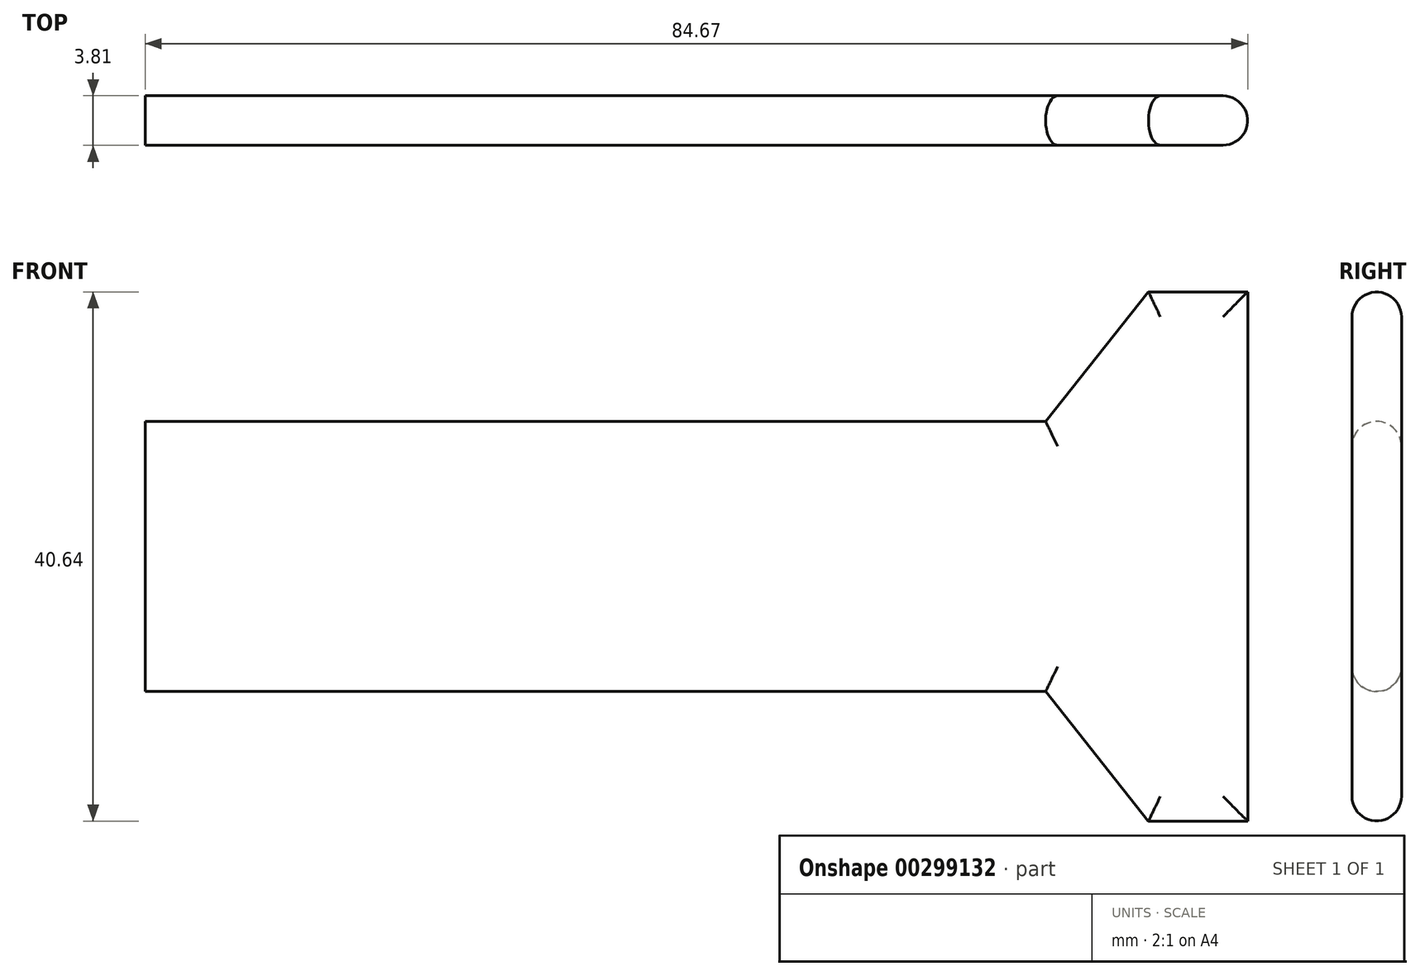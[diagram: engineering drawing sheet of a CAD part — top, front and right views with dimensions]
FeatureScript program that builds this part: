
annotation { "Feature Type Name" : "Feature", "Feature Type Description" : "" }
export const myFeature = defineFeature(function(context is Context, id is Id, definition is map)
    precondition{}
    {
        {
            var Q0;
            Q0=qCreatedBy(makeId("Front.planeOp"),FACE);
            var sketch = newSketch(context, id + "F0", { "sketchPlane" : qUnion([Q0])});
            skLineSegment(sketch, "E0", {"start": v(-30.4, 11.34) * mm, "end": v(38.74, 11.34) * mm});
            skLineSegment(sketch, "E1", {"start": v(38.74, 11.34) * mm, "end": v(38.74, -9.4) * mm});
            skLineSegment(sketch, "E2", {"start": v(38.74, -9.4) * mm, "end": v(-30.4, -9.4) * mm});
            skLineSegment(sketch, "E3", {"start": v(-30.4, -9.4) * mm, "end": v(-30.4, 11.34) * mm});
            skLineSegment(sketch, "E4", {"start": v(38.74, 11.34) * mm, "end": v(46.64, 21.29) * mm});
            skLineSegment(sketch, "E5", {"start": v(46.64, 21.29) * mm, "end": v(54.26, 21.29) * mm});
            skLineSegment(sketch, "E6", {"start": v(54.26, 21.29) * mm, "end": v(54.26, -19.35) * mm});
            skLineSegment(sketch, "E7", {"start": v(54.26, -19.35) * mm, "end": v(46.64, -19.35) * mm});
            skLineSegment(sketch, "E8", {"start": v(46.64, -19.35) * mm, "end": v(38.74, -9.4) * mm});
            skLineSegment(sketch, "E9", {"start": v(-30.4, 0) * mm, "end": v(38.74, 0) * mm});
            skSolve(sketch);
        }
        {
            var Q0;
            Q0=makeQuery(id+"F0.imprint","IMPRINT",FACE,{"disambiguationData":[TD([[makeQuery(id+"F0.imprint","IMPRINT",EDGE,{"derivedFrom":sQuery(id+"F0.wireOp",EDGE,"E1")}),1.0]])]});
            var Q1;
            {var subQ0=sQuery(id+"F0.wireOp",EDGE,"E0");Q1=makeQuery(id+"F0.imprint","IMPRINT",FACE,{"disambiguationData":[TD([[makeQuery(id+"F0.imprint","IMPRINT",EDGE,{"derivedFrom":subQ0}),-1.0]])]});}
            var Q2;
            {var subQ0=sQuery(id+"F0.wireOp",EDGE,"E2");Q2=makeQuery(id+"F0.imprint","IMPRINT",FACE,{"disambiguationData":[TD([[makeQuery(id+"F0.imprint","IMPRINT",EDGE,{"derivedFrom":subQ0}),-1.0]])]});}
            extrude(context, id + "F1", {"entities" : qUnion([Q0, Q1, Q2]), "depth" : 3.8 * mm});
        }
        {
            var Q0;
            Q0=makeQuery(id+"F1.opExtrude","CAP_EDGE",EDGE,{"disambiguationData":[OSD([sQuery(id+"F0.wireOp",EDGE,"E2")])],"isStart":true});
            var Q1;
            Q1=makeQuery(id+"F1.opExtrude","CAP_EDGE",EDGE,{"disambiguationData":[OSD([sQuery(id+"F0.wireOp",EDGE,"E0")])],"isStart":true});
            var Q2;
            Q2=makeQuery(id+"F1.opExtrude","CAP_EDGE",EDGE,{"disambiguationData":[OSD([sQuery(id+"F0.wireOp",EDGE,"E2")])],"isStart":false});
            var Q3;
            Q3=makeQuery(id+"F1.opExtrude","CAP_EDGE",EDGE,{"disambiguationData":[OSD([sQuery(id+"F0.wireOp",EDGE,"E0")])],"isStart":false});
            var Q4;
            Q4=makeQuery(id+"F1.opExtrude","CAP_EDGE",EDGE,{"disambiguationData":[OSD([sQuery(id+"F0.wireOp",EDGE,"E7")])],"isStart":false});
            var Q5;
            Q5=makeQuery(id+"F1.opExtrude","CAP_EDGE",EDGE,{"disambiguationData":[OSD([sQuery(id+"F0.wireOp",EDGE,"E7")])],"isStart":true});
            var Q6;
            Q6=makeQuery(id+"F1.opExtrude","CAP_EDGE",EDGE,{"disambiguationData":[OSD([sQuery(id+"F0.wireOp",EDGE,"E5")])],"isStart":true});
            var Q7;
            Q7=makeQuery(id+"F1.opExtrude","CAP_EDGE",EDGE,{"disambiguationData":[OSD([sQuery(id+"F0.wireOp",EDGE,"E5")])],"isStart":false});
            var Q8;
            Q8=makeQuery(id+"F1.opExtrude","CAP_EDGE",EDGE,{"disambiguationData":[OSD([sQuery(id+"F0.wireOp",EDGE,"E6")])],"isStart":false});
            var Q9;
            Q9=makeQuery(id+"F1.opExtrude","CAP_EDGE",EDGE,{"disambiguationData":[OSD([sQuery(id+"F0.wireOp",EDGE,"E6")])],"isStart":true});
            var Q10;
            Q10=makeQuery(id+"F1.opExtrude","CAP_EDGE",EDGE,{"disambiguationData":[OSD([sQuery(id+"F0.wireOp",EDGE,"E4")])],"isStart":false});
            var Q11;
            Q11=makeQuery(id+"F1.opExtrude","CAP_EDGE",EDGE,{"disambiguationData":[OSD([sQuery(id+"F0.wireOp",EDGE,"E8")])],"isStart":false});
            var Q12;
            Q12=makeQuery(id+"F1.opExtrude","CAP_EDGE",EDGE,{"disambiguationData":[OSD([sQuery(id+"F0.wireOp",EDGE,"E8")])],"isStart":true});
            var Q13;
            Q13=makeQuery(id+"F1.opExtrude","CAP_EDGE",EDGE,{"disambiguationData":[OSD([sQuery(id+"F0.wireOp",EDGE,"E4")])],"isStart":true});
            fillet(context, id + "F2", {"entities" : qUnion([Q0, Q1, Q2, Q3, Q4, Q5, Q6, Q7, Q8, Q9, Q10, Q11, Q12, Q13]), "radius" : 1.9 * mm, "tangentPropagation" : true, "allowEdgeOverflow" : false});
        }
    });
